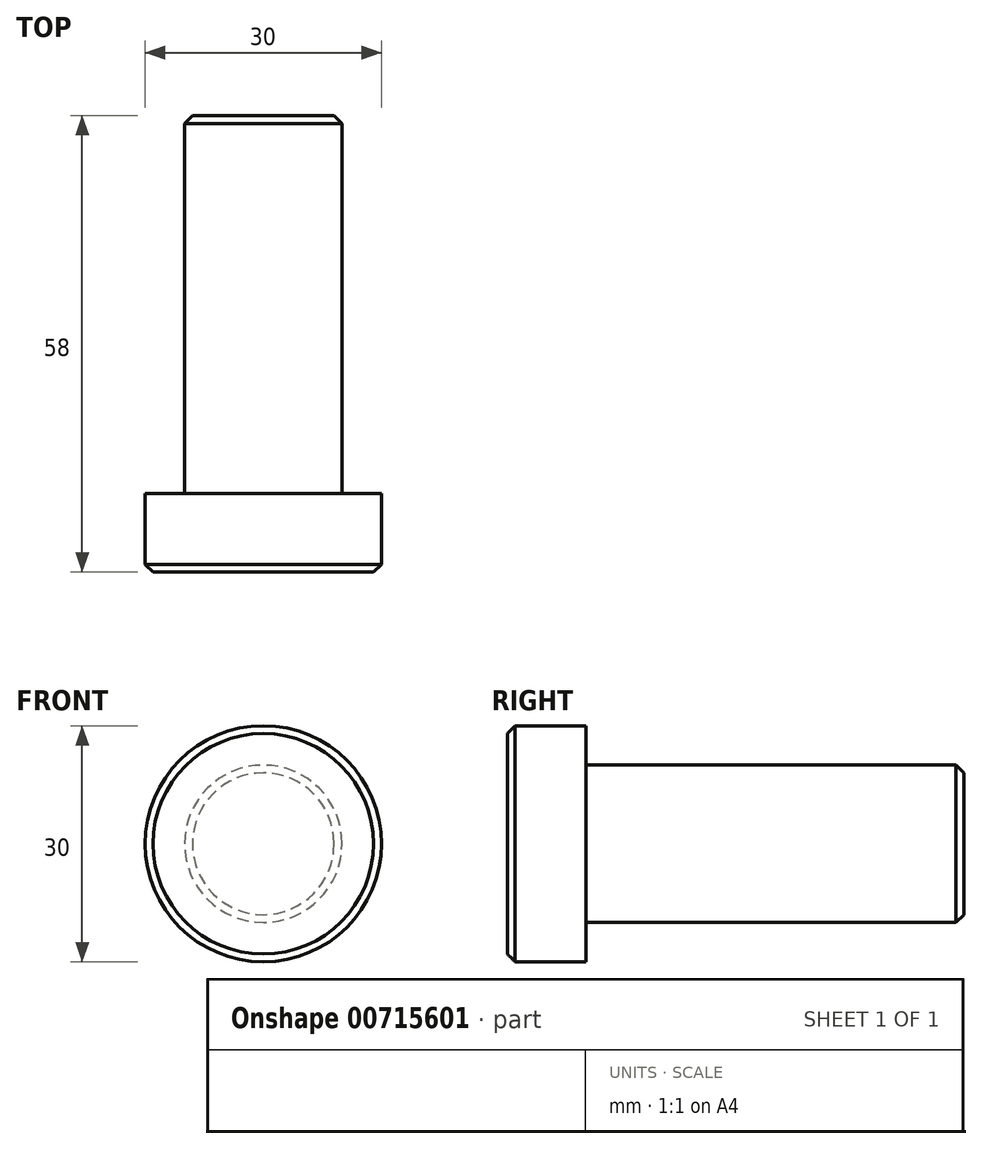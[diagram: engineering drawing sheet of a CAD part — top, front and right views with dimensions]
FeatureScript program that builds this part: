
annotation { "Feature Type Name" : "Feature", "Feature Type Description" : "" }
export const myFeature = defineFeature(function(context is Context, id is Id, definition is map)
    precondition{}
    {
        {
            var Q0;
            Q0=qCreatedBy(makeId("Front.planeOp"),FACE);
            var sketch = newSketch(context, id + "F0", { "sketchPlane" : qUnion([Q0])});
            skCircle(sketch, "E0", {"center": v(0, 0) * mm, "radius": 15 * mm});
            skSolve(sketch);
        }
        {
            var Q0;
            Q0 = qSketchRegion(id + "F0", true);
            extrude(context, id + "F1", {"entities" : qUnion([Q0]), "oppositeDirection" : true, "depth" : 10 * mm, "offsetDistance" : 25 * mm});
        }
        {
            var Q0;
            Q0=makeQuery(id+"F1.opExtrude","CAP_FACE",FACE,{"disambiguationData":[OSD([sQuery(id+"F0.wireOp",EDGE,"E0")])],"isStart":false});
            var sketch = newSketch(context, id + "F2", { "sketchPlane" : qUnion([Q0])});
            skCircle(sketch, "E1", {"center": v(0, 0) * mm, "radius": 10 * mm});
            skSolve(sketch);
        }
        {
            var Q0;
            Q0 = qSketchRegion(id + "F2", true);
            extrude(context, id + "F3", {"entities" : qUnion([Q0]), "operationType" : NewBodyOperationType.ADD, "depth" : 48 * mm, "offsetDistance" : 25 * mm});
        }
        {
            var Q0;
            Q0=makeQuery(id+"F3.opExtrude","CAP_EDGE",EDGE,{"disambiguationData":[OSD([sQuery(id+"F2.wireOp",EDGE,"E1")])],"isStart":false});
            var Q1;
            Q1=makeQuery(id+"F1.opExtrude","CAP_EDGE",EDGE,{"disambiguationData":[OSD([sQuery(id+"F0.wireOp",EDGE,"E0")])],"isStart":true});
            chamfer(context, id + "F4", {"entities" : qUnion([Q0, Q1]), "width" : 1 * mm, "tangentPropagation" : true});
        }
    });
